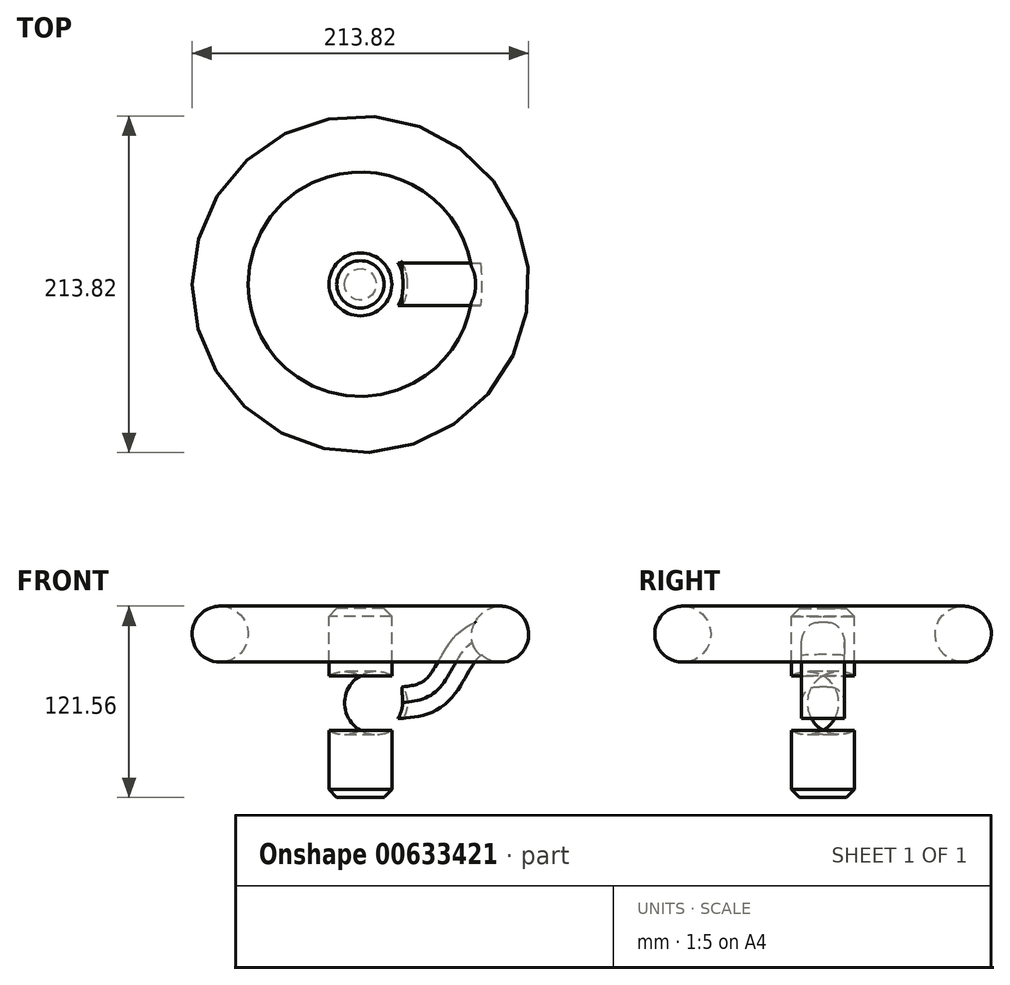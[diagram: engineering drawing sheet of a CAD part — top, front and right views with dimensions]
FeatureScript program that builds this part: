
annotation { "Feature Type Name" : "Feature", "Feature Type Description" : "" }
export const myFeature = defineFeature(function(context is Context, id is Id, definition is map)
    precondition{}
    {
        {
            var Q0;
            Q0=qCreatedBy(makeId("Front.planeOp"),FACE);
            var sketch = newSketch(context, id + "F0", { "sketchPlane" : qUnion([Q0])});
            skLineSegment(sketch, "E0", {"start": v(0, 60) * mm, "end": v(0, -60) * mm});
            skLineSegment(sketch, "E1", {"start": v(0, -60) * mm, "end": v(20, -60) * mm});
            skLineSegment(sketch, "E2", {"start": v(20, -60) * mm, "end": v(20, -17.32) * mm});
            skLineSegment(sketch, "E3", {"start": v(0, 60) * mm, "end": v(20, 60) * mm});
            skLineSegment(sketch, "E4", {"start": v(20, 60) * mm, "end": v(20, 17.32) * mm});
            skArc(sketch, "E5", {"start": v(20, -17.32) * mm, "mid": v(30, 0) * mm, "end": v(20, 17.32) * mm});
            skSolve(sketch);
        }
        {
            var Q0;
            Q0=makeQuery(id+"F0.imprint","IMPRINT",FACE,{"disambiguationData":[TD([[makeQuery(id+"F0.imprint","IMPRINT",EDGE,{"derivedFrom":sQuery(id+"F0.wireOp",EDGE,"E0")}),1.0]])]});
            var Q1;
            Q1=sQuery(id+"F0.wireOp",EDGE,"E0");
            revolve(context, id + "F1", {"entities" : qUnion([Q0]), "axis" : qUnion([Q1]), "revolveType" : RevolveType.FULL});
        }
        {
            var Q0;
            Q0=makeQuery(id+"F1.opRevolve","SWEPT_EDGE",EDGE,{"disambiguationData":[OSD([sQuery(id+"F0.wireOp",EDGE,"E3"),sQuery(id+"F0.wireOp",EDGE,"E4")])]});
            chamfer(context, id + "F2", {"entities" : qUnion([Q0]), "width" : 5 * mm, "tangentPropagation" : true});
        }
        {
            var Q0;
            Q0=makeQuery(id+"F1.opRevolve","SWEPT_EDGE",EDGE,{"disambiguationData":[OSD([sQuery(id+"F0.wireOp",EDGE,"E1"),sQuery(id+"F0.wireOp",EDGE,"E2")])]});
            chamfer(context, id + "F3", {"entities" : qUnion([Q0]), "width" : 5 * mm, "tangentPropagation" : true});
        }
        {
            var Q0;
            Q0=qCreatedBy(makeId("Right.planeOp"),FACE);
            cPlane(context, id + "F4", {"entities" : qUnion([Q0]), "cplaneType" : CPlaneType.OFFSET, "offset" : 20 * mm, "width" : 150 * mm, "height" : 150 * mm});
        }
        {
            var Q0;
            Q0=qCreatedBy(id+"F4.planeOp",FACE);
            var sketch = newSketch(context, id + "F5", { "sketchPlane" : qUnion([Q0])});
            skLineSegment(sketch, "E6.bottom", {"start": v(3.61, 10) * mm, "end": v(-3.61, 10) * mm});
            skLineSegment(sketch, "E6.top", {"start": v(13.61, -10) * mm, "end": v(-13.61, -10) * mm});
            skLineSegment(sketch, "E6.left", {"start": v(13.61, 0) * mm, "end": v(13.61, -10) * mm});
            skLineSegment(sketch, "E6.right", {"start": v(-13.61, 0) * mm, "end": v(-13.61, -10) * mm});
            skPoint(sketch, "E6.middle", {"position": v(0, 0) * mm});
            skPoint(sketch, "E7.visualSharp", {"position": v(-13.61, 10) * mm});
            skArc(sketch, "E7.filletArc", {"start": v(-3.61, 10) * mm, "mid": v(-10.68, 7.07) * mm, "end": v(-13.61, 0) * mm});
            skPoint(sketch, "E8.visualSharp", {"position": v(13.61, 10) * mm});
            skArc(sketch, "E8.filletArc", {"start": v(13.61, 0) * mm, "mid": v(10.68, 7.07) * mm, "end": v(3.61, 10) * mm});
            skSolve(sketch);
        }
        {
            var Q0;
            Q0=qCreatedBy(makeId("Front.planeOp"),FACE);
            var sketch = newSketch(context, id + "F6", { "sketchPlane" : qUnion([Q0])});
            skFitSpline(sketch, "E9", {"points": [v(20.05, 0) * mm, v(47.7, 7.17) * mm, v(67.85, 35.96) * mm, v(88.58, 45.75) * mm], "startDerivative": vector(91.41, 3.91) * mm, "endDerivative": vector(74.94, 18.38) * mm});
            skSolve(sketch);
        }
        {
            var Q0;
            Q0 = qSketchRegion(id + "F5", true);
            var Q1;
            Q1 = qConstructionFilter(qBodyType(qCreatedBy(id + "F6" ,EDGE), BodyType.WIRE), ConstructionObject.NO);
            sweep(context, id + "F7", {"operationType" : NewBodyOperationType.ADD, "profiles" : qUnion([Q0]), "path" : qUnion([Q1])});
        }
        {
            var Q0;
            Q0=qCreatedBy(makeId("Front.planeOp"),FACE);
            var sketch = newSketch(context, id + "F8", { "sketchPlane" : qUnion([Q0])});
            skCircle(sketch, "E10", {"center": v(89.11, 43.76) * mm, "radius": 17.8 * mm});
            skSolve(sketch);
        }
        {
            var Q0;
            Q0=makeQuery(id+"F8.imprint","IMPRINT",FACE,{"disambiguationData":[TD([[makeQuery(id+"F8.imprint","IMPRINT",EDGE,{"derivedFrom":sQuery(id+"F8.wireOp",EDGE,"E10")}),1.0]])]});
            var Q1;
            Q1=sQuery(id+"F0.wireOp",EDGE,"E0");
            revolve(context, id + "F9", {"operationType" : NewBodyOperationType.ADD, "entities" : qUnion([Q0]), "axis" : qUnion([Q1]), "revolveType" : RevolveType.FULL});
        }
    });
